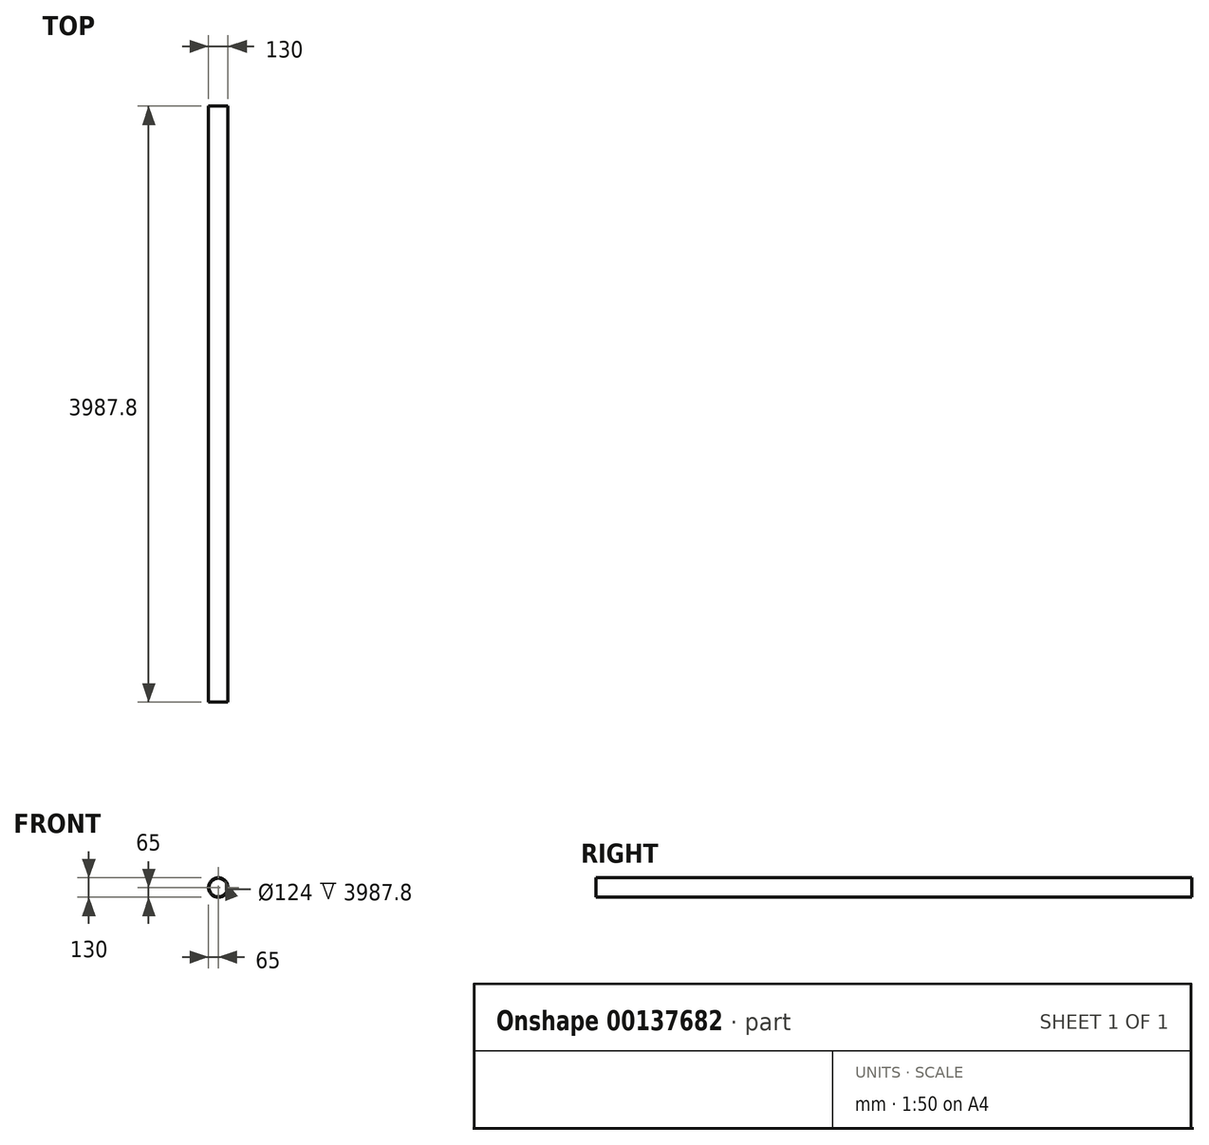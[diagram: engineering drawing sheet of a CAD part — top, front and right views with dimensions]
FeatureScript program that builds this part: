
annotation { "Feature Type Name" : "Feature", "Feature Type Description" : "" }
export const myFeature = defineFeature(function(context is Context, id is Id, definition is map)
    precondition{}
    {
        {
            var Q0;
            Q0=qCreatedBy(makeId("Front.planeOp"),FACE);
            var sketch = newSketch(context, id + "F0", { "sketchPlane" : qUnion([Q0])});
            skCircle(sketch, "E0", {"center": v(0, 0) * mm, "radius": 65 * mm});
            skCircle(sketch, "E1", {"center": v(0, 0) * mm, "radius": 62 * mm});
            skSolve(sketch);
        }
        {
            var Q0;
            Q0=makeQuery(id+"F0.imprint","IMPRINT",FACE,{"disambiguationData":[TD([[makeQuery(id+"F0.imprint","IMPRINT",EDGE,{"derivedFrom":sQuery(id+"F0.wireOp",EDGE,"E0")}),1.0]])]});
            extrude(context, id + "F1", {"entities" : qUnion([Q0]), "depth" : 3987.8 * mm});
        }
    });
